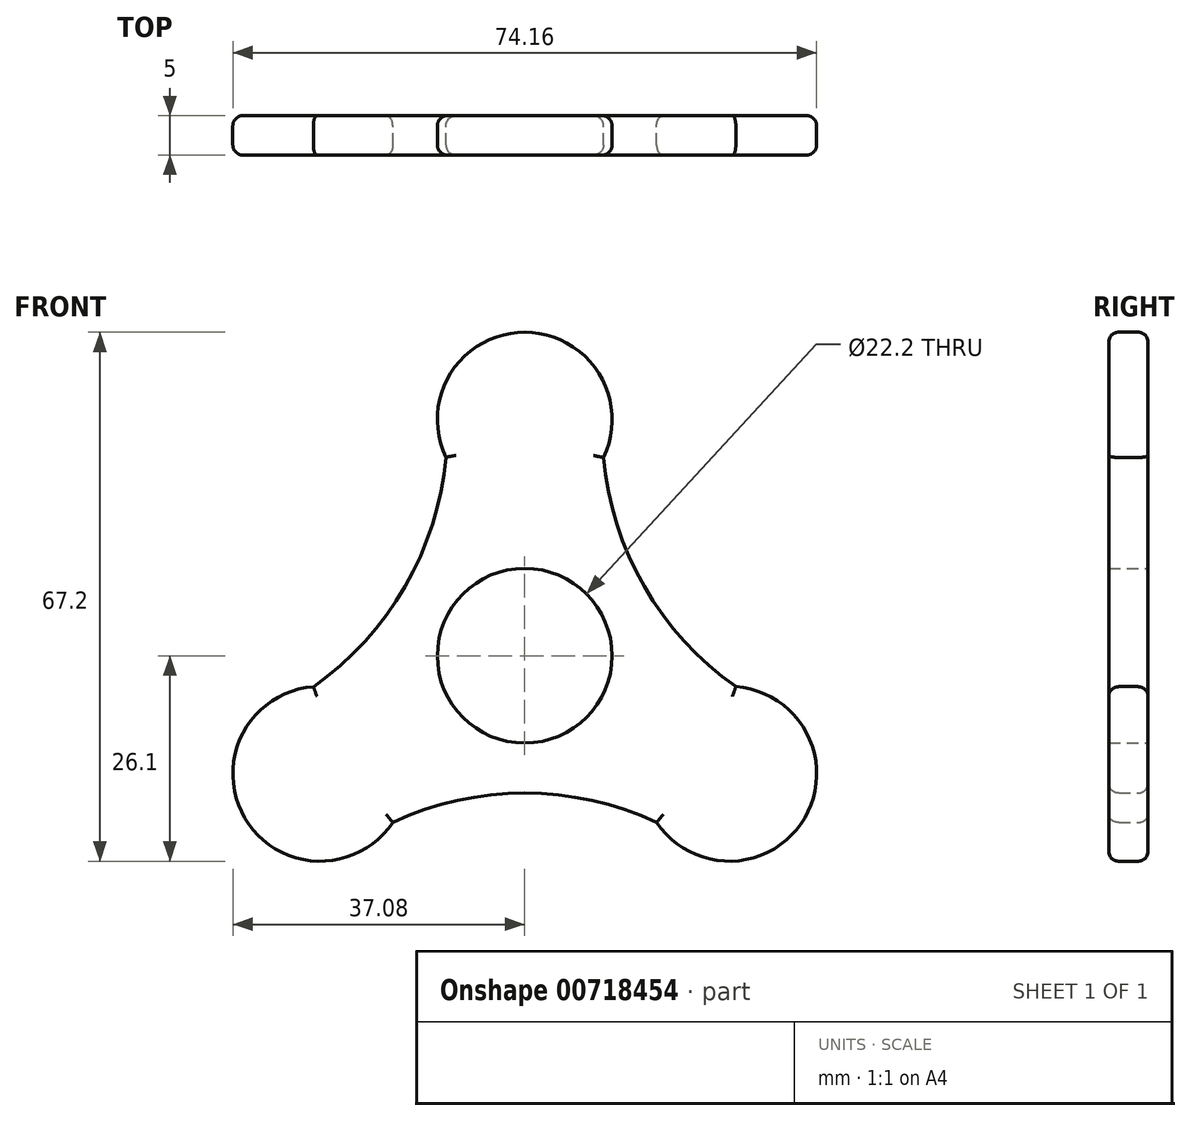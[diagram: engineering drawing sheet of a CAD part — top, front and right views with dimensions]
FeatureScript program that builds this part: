
annotation { "Feature Type Name" : "Feature", "Feature Type Description" : "" }
export const myFeature = defineFeature(function(context is Context, id is Id, definition is map)
    precondition{}
    {
        {
            var Q0;
            Q0=qCreatedBy(makeId("Front.planeOp"),FACE);
            var sketch = newSketch(context, id + "F0", { "sketchPlane" : qUnion([Q0])});
            skCircle(sketch, "E0", {"center": v(0, 0) * mm, "radius": 11.1 * mm});
            skArc(sketch, "E1", {"start": v(10, 25.19) * mm, "mid": v(0.01, 41.1) * mm, "end": v(-10.01, 25.21) * mm});
            skArc(sketch, "E2.1.0", {"start": v(-26.84, -3.93) * mm, "mid": v(-35.56, -20.6) * mm, "end": v(-16.76, -21.17) * mm});
            skArc(sketch, "E2.2.0", {"start": v(16.76, -21.17) * mm, "mid": v(35.57, -20.6) * mm, "end": v(26.82, -3.93) * mm});
            skArc(sketch, "E3", {"start": v(-34.82, -8.28) * mm, "mid": v(-15.21, 8.78) * mm, "end": v(-10.24, 34.3) * mm});
            skArc(sketch, "E4", {"start": v(10.24, 34.3) * mm, "mid": v(15.2, 8.77) * mm, "end": v(34.82, -8.28) * mm});
            skArc(sketch, "E5", {"start": v(24.58, -26.01) * mm, "mid": v(0, -17.45) * mm, "end": v(-24.58, -26.01) * mm});
            skSolve(sketch);
        }
        {
            var Q0;
            Q0 = qSketchRegion(id + "F0", true);
            extrude(context, id + "F1", {"entities" : qUnion([Q0]), "depth" : 5 * mm, "offsetDistance" : 25 * mm});
        }
        {
            var Q0;
            Q0=makeQuery(id+"F1.opExtrude","CAP_EDGE",EDGE,{"disambiguationData":[OSD([sQuery(id+"F0.wireOp",EDGE,"E3")])],"isStart":false});
            var Q1;
            Q1=makeQuery(id+"F1.opExtrude","CAP_EDGE",EDGE,{"disambiguationData":[OSD([sQuery(id+"F0.wireOp",EDGE,"E4")])],"isStart":false});
            var Q2;
            Q2=makeQuery(id+"F1.opExtrude","CAP_EDGE",EDGE,{"disambiguationData":[OSD([sQuery(id+"F0.wireOp",EDGE,"E5")])],"isStart":false});
            var Q3;
            Q3=makeQuery(id+"F1.opExtrude","CAP_EDGE",EDGE,{"disambiguationData":[OSD([sQuery(id+"F0.wireOp",EDGE,"E1")])],"isStart":false});
            var Q4;
            Q4=makeQuery(id+"F1.opExtrude","CAP_EDGE",EDGE,{"disambiguationData":[OSD([sQuery(id+"F0.wireOp",EDGE,"E2.1.0")])],"isStart":false});
            var Q5;
            Q5=makeQuery(id+"F1.opExtrude","CAP_EDGE",EDGE,{"disambiguationData":[OSD([sQuery(id+"F0.wireOp",EDGE,"E2.2.0")])],"isStart":false});
            fillet(context, id + "F2", {"entities" : qUnion([Q0, Q1, Q2, Q3, Q4, Q5]), "radius" : 1.27 * mm, "tangentPropagation" : true, "allowEdgeOverflow" : false});
        }
        {
            var Q0;
            Q0=makeQuery(id+"F1.opExtrude","CAP_EDGE",EDGE,{"disambiguationData":[OSD([sQuery(id+"F0.wireOp",EDGE,"E1")])],"isStart":true});
            var Q1;
            Q1=makeQuery(id+"F1.opExtrude","CAP_EDGE",EDGE,{"disambiguationData":[OSD([sQuery(id+"F0.wireOp",EDGE,"E4")])],"isStart":true});
            var Q2;
            Q2=makeQuery(id+"F1.opExtrude","CAP_EDGE",EDGE,{"disambiguationData":[OSD([sQuery(id+"F0.wireOp",EDGE,"E2.2.0")])],"isStart":true});
            var Q3;
            Q3=makeQuery(id+"F1.opExtrude","CAP_EDGE",EDGE,{"disambiguationData":[OSD([sQuery(id+"F0.wireOp",EDGE,"E5")])],"isStart":true});
            var Q4;
            Q4=makeQuery(id+"F1.opExtrude","CAP_EDGE",EDGE,{"disambiguationData":[OSD([sQuery(id+"F0.wireOp",EDGE,"E2.1.0")])],"isStart":true});
            var Q5;
            Q5=makeQuery(id+"F1.opExtrude","CAP_EDGE",EDGE,{"disambiguationData":[OSD([sQuery(id+"F0.wireOp",EDGE,"E3")])],"isStart":true});
            fillet(context, id + "F3", {"entities" : qUnion([Q0, Q1, Q2, Q3, Q4, Q5]), "radius" : 1.27 * mm, "tangentPropagation" : true, "allowEdgeOverflow" : false});
        }
    });
